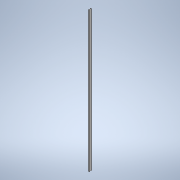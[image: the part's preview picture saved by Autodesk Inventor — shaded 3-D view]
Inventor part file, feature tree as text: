
AUTODESK INVENTOR PART (.ipt)
format: ipt  version: 2020 (Build 240168000, 168)  size: 130,048 bytes
history: native  units: in
note: dims shown in document units (in); Inventor stores cm internally (conversion verified against a paired STEP export)
features: extrude x1, sketch x1, other x1, projected_geometry x1
ambient origin geometry x8: Origin, YZ Plane, XZ Plane, XY Plane, X Axis, Y Axis, Z Axis, Center Point
bodies: Solid1 (feature_tree)
feature tree (4):
  extrude  "Extrusion1"  [1 undecoded]
  sketch  "Sketch1"  dims[d0=488.189in d1=0.0in]
  other  "AISC - W 8x15 - 118,11024_1:1"
  projected_geometry  "Project Cut Edges1"
note: 1 required parameter value undecoded (feature->parameter linkage not recoverable at this tier; creation-order binding heuristic only, values carry confidence <= 0.55)
